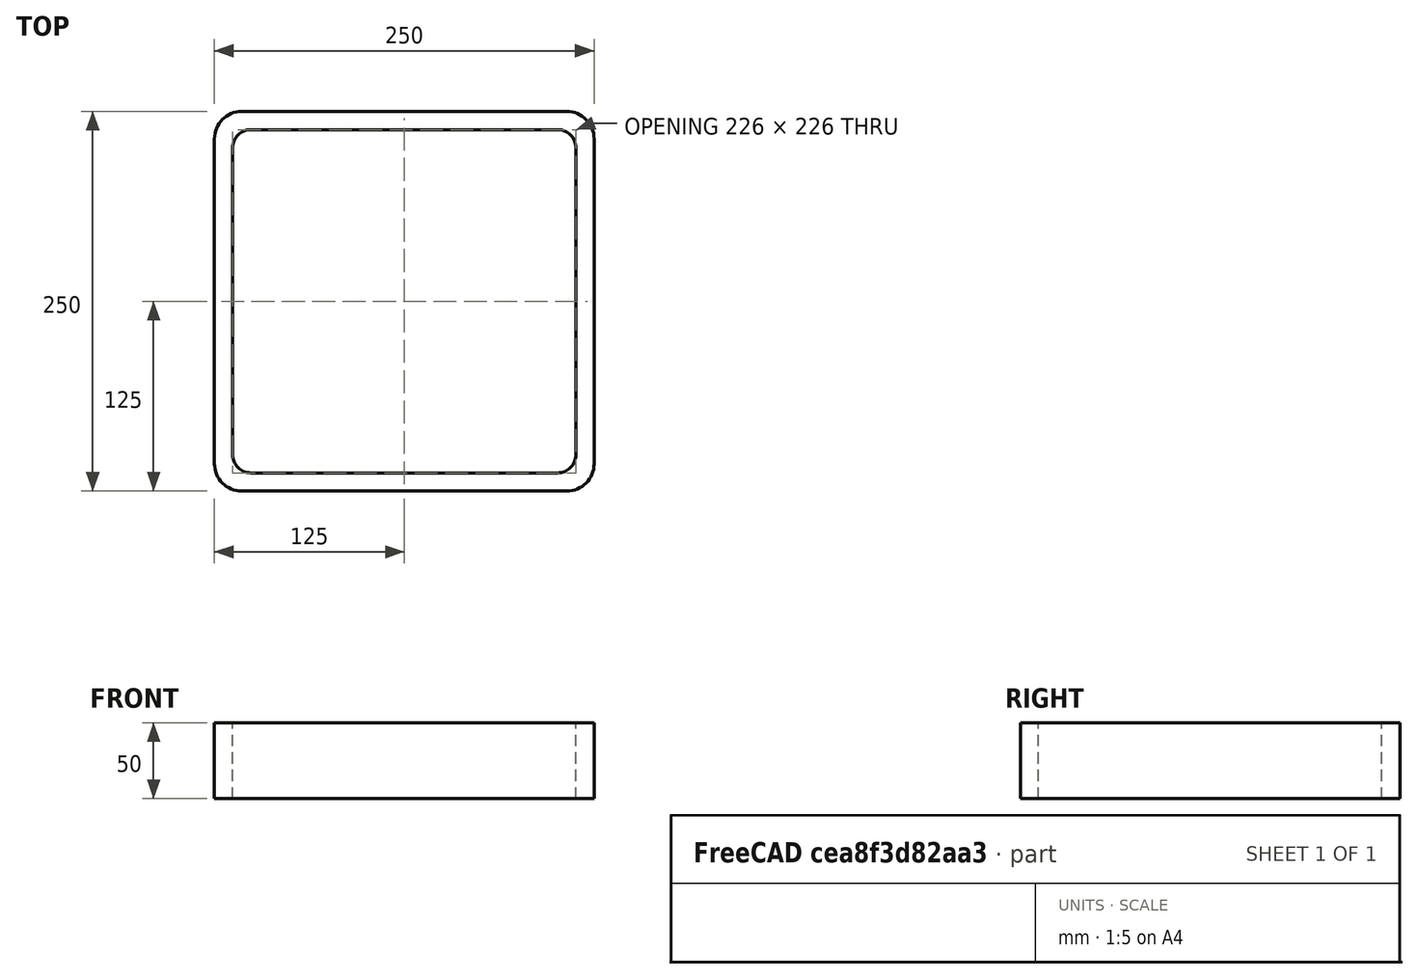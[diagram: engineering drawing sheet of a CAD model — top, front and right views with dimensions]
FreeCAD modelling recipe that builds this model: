
FCSTD DOCUMENT  (FreeCAD 0.15R4671 (Git))
Label: Square hollow section 250x250x12 EN10219 S235JRH
License: All rights reserved
LicenseURL: http://en.wikipedia.org/wiki/All_rights_reserved
objects: Sketcher::SketchObject×1, Part::Extrusion×1
note: 2 computed .brp shape members not serialized (recipe doc carries the construction recipe); baked Part::Feature solids carry a one-line shape summary decoded from their .brp

FEATURE [Sketcher::SketchObject] Sketch
  sketch-geometry (16):
    g0: LineSegment StartX=-101 StartY=113 StartZ=0 EndX=101 EndY=113 EndZ=0
    g1: LineSegment StartX=113 StartY=101 StartZ=0 EndX=113 EndY=-101 EndZ=0
    g2: LineSegment StartX=101 StartY=-113 StartZ=0 EndX=-101 EndY=-113 EndZ=0
    g3: LineSegment StartX=-113 StartY=-101 StartZ=0 EndX=-113 EndY=101 EndZ=0
    g4: LineSegment StartX=-107 StartY=125 StartZ=0 EndX=107 EndY=125 EndZ=0
    g5: LineSegment StartX=125 StartY=107 StartZ=0 EndX=125 EndY=-107 EndZ=0
    g6: LineSegment StartX=107 StartY=-125 StartZ=0 EndX=-107 EndY=-125 EndZ=0
    g7: LineSegment StartX=-125 StartY=-107 StartZ=0 EndX=-125 EndY=107 EndZ=0
    g8: ArcOfCircle CenterX=-101 CenterY=101 CenterZ=0 NormalX=0 NormalY=0 NormalZ=1 Radius=12 StartAngle=1.5708 EndAngle=3.14159
    g9: ArcOfCircle CenterX=101 CenterY=101 CenterZ=0 NormalX=0 NormalY=0 NormalZ=1 Radius=12 StartAngle=0 EndAngle=1.5708
    g10: ArcOfCircle CenterX=101 CenterY=-101 CenterZ=0 NormalX=0 NormalY=0 NormalZ=1 Radius=12 StartAngle=4.71239 EndAngle=6.28319
    g11: ArcOfCircle CenterX=-101 CenterY=-101 CenterZ=0 NormalX=0 NormalY=0 NormalZ=1 Radius=12 StartAngle=3.14159 EndAngle=4.71239
    g12: ArcOfCircle CenterX=107 CenterY=107 CenterZ=0 NormalX=0 NormalY=0 NormalZ=1 Radius=18 StartAngle=0 EndAngle=1.5708
    g13: ArcOfCircle CenterX=107 CenterY=-107 CenterZ=0 NormalX=0 NormalY=0 NormalZ=1 Radius=18 StartAngle=4.71239 EndAngle=6.28319
    g14: ArcOfCircle CenterX=-107 CenterY=-107 CenterZ=0 NormalX=0 NormalY=0 NormalZ=1 Radius=18 StartAngle=3.14159 EndAngle=4.71239
    g15: ArcOfCircle CenterX=-107 CenterY=107 CenterZ=0 NormalX=0 NormalY=0 NormalZ=1 Radius=18 StartAngle=1.5708 EndAngle=3.14159
  constraints (36):
    c: Horizontal(g2)
    c: Vertical(g3)
    c: Horizontal(g6)
    c: Vertical(g7)
    c: Tangent(g3,g8) = 1.5708
    c: Tangent(g0,g8) = 1.5708
    c: Tangent(g0,g9) = 1.5708
    c: Tangent(g1,g9) = 1.5708
    c: Tangent(g1,g10) = 1.5708
    c: Tangent(g2,g10) = 1.5708
    c: Tangent(g2,g11) = 1.5708
    c: Tangent(g3,g11) = 1.5708
    c: Tangent(g4,g12) = 1.5708
    c: Tangent(g5,g12) = 1.5708
    c: Tangent(g5,g13) = 1.5708
    c: Tangent(g6,g13) = 1.5708
    c: Tangent(g6,g14) = 1.5708
    c: Tangent(g7,g14) = 1.5708
    c: Tangent(g7,g15) = 1.5708
    c: Tangent(g4,g15) = 1.5708
    c: Equal(g9,g8)
    c: Equal(g9,g11)
    c: Equal(g9,g10)
    c: Equal(g12,g15)
    c: Equal(g12,g14)
    c: Equal(g12,g13)
    c: Symmetric(g4,g6,g-1)
    c: Symmetric(g7,g5,g-2)
    c: DistanceY(g4,g6) = -250
    c: DistanceX(g7,g5) = 250
    c: Symmetric(g3,g1,g-2)
    c: Symmetric(g0,g2,g-1)
    c: DistanceY(g0,g4) = 12
    c: DistanceX(g5,g1) = -12
    c: Radius(g9) = 12
    c: Radius(g12) = 18
FEATURE [Part::Extrusion] Extrude  label="Square hollow section 250x250x12 EN10219 S235JRH"
  Base = -> Sketch
  Dir = (0,0,50)
  Solid = true
